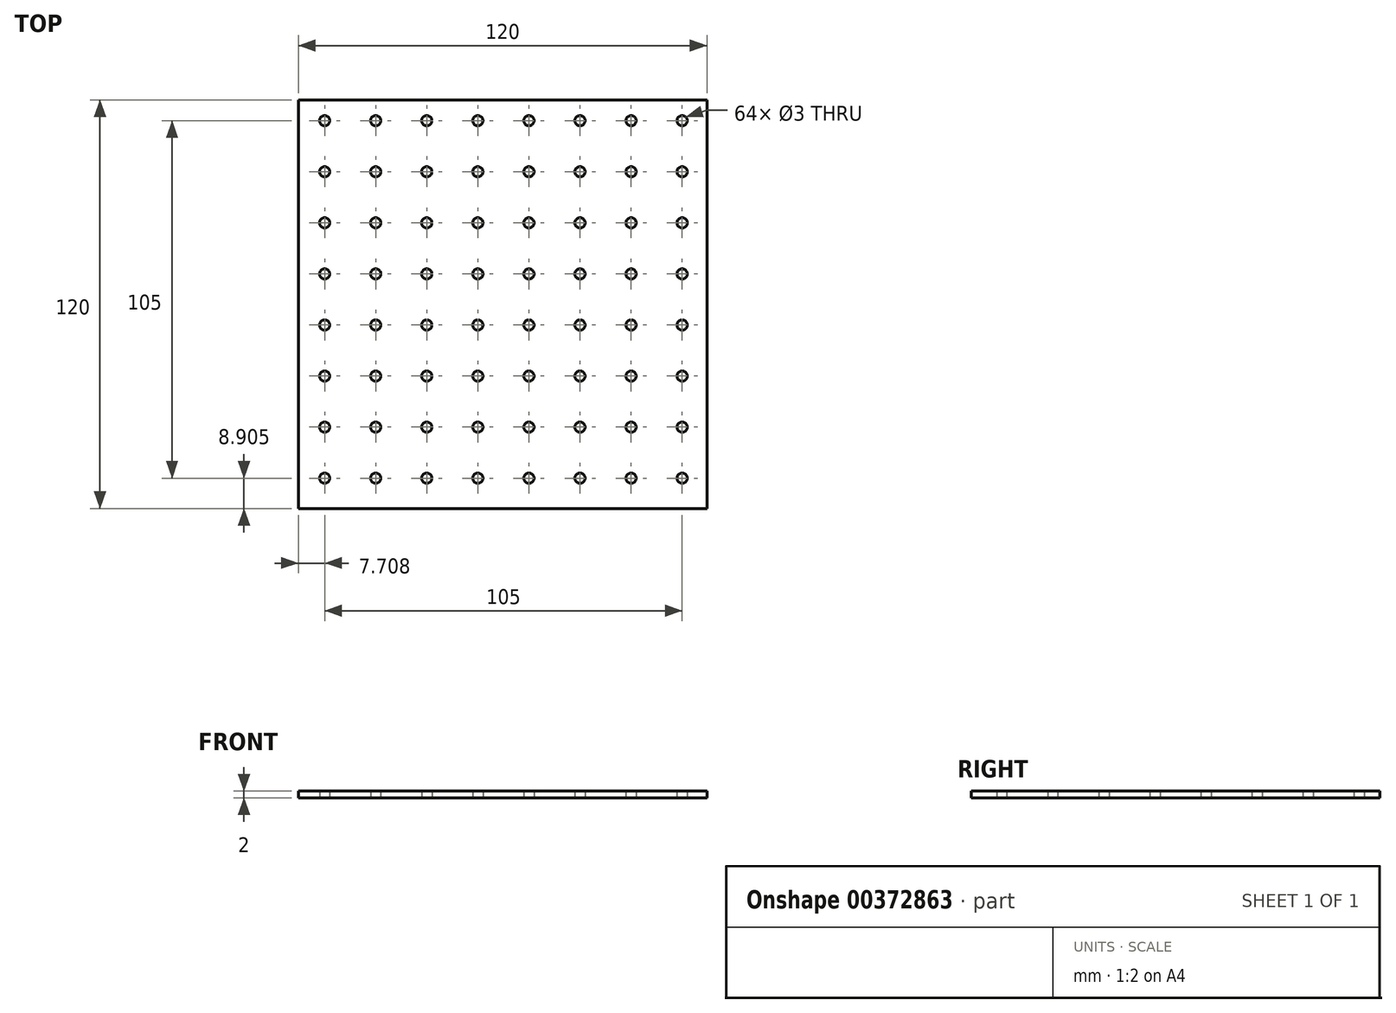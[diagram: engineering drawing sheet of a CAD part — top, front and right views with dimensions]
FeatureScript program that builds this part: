
annotation { "Feature Type Name" : "Feature", "Feature Type Description" : "" }
export const myFeature = defineFeature(function(context is Context, id is Id, definition is map)
    precondition{}
    {
        {
            var Q0;
            Q0=qCreatedBy(makeId("Top.planeOp"),FACE);
            var sketch = newSketch(context, id + "F0", { "sketchPlane" : qUnion([Q0])});
            skCircle(sketch, "E0", {"center": v(-48.08, 34.11) * mm, "radius": 1.5 * mm});
            skCircle(sketch, "E1", {"center": v(-33.08, 34.11) * mm, "radius": 1.5 * mm});
            skCircle(sketch, "E2", {"center": v(-18.08, 34.11) * mm, "radius": 1.5 * mm});
            skCircle(sketch, "E3", {"center": v(-3.08, 34.11) * mm, "radius": 1.5 * mm});
            skCircle(sketch, "E4", {"center": v(11.92, 34.11) * mm, "radius": 1.5 * mm});
            skCircle(sketch, "E5", {"center": v(26.92, 34.11) * mm, "radius": 1.5 * mm});
            skCircle(sketch, "E6", {"center": v(41.92, 34.11) * mm, "radius": 1.5 * mm});
            skCircle(sketch, "E7", {"center": v(56.92, 34.11) * mm, "radius": 1.5 * mm});
            skCircle(sketch, "E8", {"center": v(-48.08, 19.11) * mm, "radius": 1.5 * mm});
            skCircle(sketch, "E9", {"center": v(-33.08, 19.11) * mm, "radius": 1.5 * mm});
            skCircle(sketch, "E10", {"center": v(-18.08, 19.11) * mm, "radius": 1.5 * mm});
            skCircle(sketch, "E11", {"center": v(-3.08, 19.11) * mm, "radius": 1.5 * mm});
            skCircle(sketch, "E12", {"center": v(11.92, 19.11) * mm, "radius": 1.5 * mm});
            skCircle(sketch, "E13", {"center": v(26.92, 19.11) * mm, "radius": 1.5 * mm});
            skCircle(sketch, "E14", {"center": v(41.92, 19.11) * mm, "radius": 1.5 * mm});
            skCircle(sketch, "E15", {"center": v(56.92, 19.11) * mm, "radius": 1.5 * mm});
            skCircle(sketch, "E16", {"center": v(-48.08, 4.11) * mm, "radius": 1.5 * mm});
            skCircle(sketch, "E17", {"center": v(-33.08, 4.11) * mm, "radius": 1.5 * mm});
            skCircle(sketch, "E18", {"center": v(-18.08, 4.11) * mm, "radius": 1.5 * mm});
            skCircle(sketch, "E19", {"center": v(-3.08, 4.11) * mm, "radius": 1.5 * mm});
            skCircle(sketch, "E20", {"center": v(11.92, 4.11) * mm, "radius": 1.5 * mm});
            skCircle(sketch, "E21", {"center": v(26.92, 4.11) * mm, "radius": 1.5 * mm});
            skCircle(sketch, "E22", {"center": v(41.92, 4.11) * mm, "radius": 1.5 * mm});
            skCircle(sketch, "E23", {"center": v(56.92, 4.11) * mm, "radius": 1.5 * mm});
            skCircle(sketch, "E24", {"center": v(-48.08, -10.89) * mm, "radius": 1.5 * mm});
            skCircle(sketch, "E25", {"center": v(-33.08, -10.89) * mm, "radius": 1.5 * mm});
            skCircle(sketch, "E26", {"center": v(-18.08, -10.89) * mm, "radius": 1.5 * mm});
            skCircle(sketch, "E27", {"center": v(-3.08, -10.89) * mm, "radius": 1.5 * mm});
            skCircle(sketch, "E28", {"center": v(11.92, -10.89) * mm, "radius": 1.5 * mm});
            skCircle(sketch, "E29", {"center": v(26.92, -10.89) * mm, "radius": 1.5 * mm});
            skCircle(sketch, "E30", {"center": v(41.92, -10.89) * mm, "radius": 1.5 * mm});
            skCircle(sketch, "E31", {"center": v(56.92, -10.89) * mm, "radius": 1.5 * mm});
            skCircle(sketch, "E32", {"center": v(-48.08, -25.89) * mm, "radius": 1.5 * mm});
            skCircle(sketch, "E33", {"center": v(-33.08, -25.89) * mm, "radius": 1.5 * mm});
            skCircle(sketch, "E34", {"center": v(-18.08, -25.89) * mm, "radius": 1.5 * mm});
            skCircle(sketch, "E35", {"center": v(-3.08, -25.89) * mm, "radius": 1.5 * mm});
            skCircle(sketch, "E36", {"center": v(11.92, -25.89) * mm, "radius": 1.5 * mm});
            skCircle(sketch, "E37", {"center": v(26.92, -25.89) * mm, "radius": 1.5 * mm});
            skCircle(sketch, "E38", {"center": v(41.92, -25.89) * mm, "radius": 1.5 * mm});
            skCircle(sketch, "E39", {"center": v(56.92, -25.89) * mm, "radius": 1.5 * mm});
            skCircle(sketch, "E40", {"center": v(-48.08, -40.89) * mm, "radius": 1.5 * mm});
            skCircle(sketch, "E41", {"center": v(-33.08, -40.89) * mm, "radius": 1.5 * mm});
            skCircle(sketch, "E42", {"center": v(-18.08, -40.89) * mm, "radius": 1.5 * mm});
            skCircle(sketch, "E43", {"center": v(-3.08, -40.89) * mm, "radius": 1.5 * mm});
            skCircle(sketch, "E44", {"center": v(11.92, -40.89) * mm, "radius": 1.5 * mm});
            skCircle(sketch, "E45", {"center": v(26.92, -40.89) * mm, "radius": 1.5 * mm});
            skCircle(sketch, "E46", {"center": v(41.92, -40.89) * mm, "radius": 1.5 * mm});
            skCircle(sketch, "E47", {"center": v(56.92, -40.89) * mm, "radius": 1.5 * mm});
            skCircle(sketch, "E48", {"center": v(-48.08, -55.89) * mm, "radius": 1.5 * mm});
            skCircle(sketch, "E49", {"center": v(-33.08, -55.89) * mm, "radius": 1.5 * mm});
            skCircle(sketch, "E50", {"center": v(-18.08, -55.89) * mm, "radius": 1.5 * mm});
            skCircle(sketch, "E51", {"center": v(-3.08, -55.89) * mm, "radius": 1.5 * mm});
            skCircle(sketch, "E52", {"center": v(11.92, -55.89) * mm, "radius": 1.5 * mm});
            skCircle(sketch, "E53", {"center": v(26.92, -55.89) * mm, "radius": 1.5 * mm});
            skCircle(sketch, "E54", {"center": v(41.92, -55.89) * mm, "radius": 1.5 * mm});
            skCircle(sketch, "E55", {"center": v(56.92, -55.89) * mm, "radius": 1.5 * mm});
            skCircle(sketch, "E56", {"center": v(-48.08, -70.89) * mm, "radius": 1.5 * mm});
            skCircle(sketch, "E57", {"center": v(-33.08, -70.89) * mm, "radius": 1.5 * mm});
            skCircle(sketch, "E58", {"center": v(-18.08, -70.89) * mm, "radius": 1.5 * mm});
            skCircle(sketch, "E59", {"center": v(-3.08, -70.89) * mm, "radius": 1.5 * mm});
            skCircle(sketch, "E60", {"center": v(11.92, -70.89) * mm, "radius": 1.5 * mm});
            skCircle(sketch, "E61", {"center": v(26.92, -70.89) * mm, "radius": 1.5 * mm});
            skCircle(sketch, "E62", {"center": v(41.92, -70.89) * mm, "radius": 1.5 * mm});
            skCircle(sketch, "E63", {"center": v(56.92, -70.89) * mm, "radius": 1.5 * mm});
            skLineSegment(sketch, "E64.bottom", {"start": v(-55.79, 40.2) * mm, "end": v(64.21, 40.2) * mm});
            skLineSegment(sketch, "E64.top", {"start": v(-55.79, -79.8) * mm, "end": v(64.21, -79.8) * mm});
            skLineSegment(sketch, "E64.left", {"start": v(-55.79, 40.2) * mm, "end": v(-55.79, -79.8) * mm});
            skLineSegment(sketch, "E64.right", {"start": v(64.21, 40.2) * mm, "end": v(64.21, -79.8) * mm});
            skSolve(sketch);
        }
        {
            var Q0;
            Q0=makeQuery(id+"F0.imprint","IMPRINT",FACE,{"disambiguationData":[TD([[makeQuery(id+"F0.imprint","IMPRINT",EDGE,{"derivedFrom":sQuery(id+"F0.wireOp",EDGE,"E0")}),-1.0]])]});
            extrude(context, id + "F1", {"entities" : qUnion([Q0]), "depth" : 2 * mm});
        }
    });
